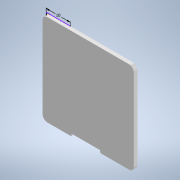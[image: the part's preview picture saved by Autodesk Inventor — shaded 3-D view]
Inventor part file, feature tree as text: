
AUTODESK INVENTOR PART (.ipt)
format: ipt  version: 2022 (Build 260153000, 153)  size: 134,144 bytes
history: native  units: mm
features: sketch x3, other x2, extrude x2, fillet x2
ambient origin geometry x8: Origin, YZ Plane, XZ Plane, XY Plane, X Axis, Y Axis, Z Axis, Center Point
bodies: Body1 (feature_tree)
feature tree (9):
  other  "Твердое тело1"
  other  "РабПлоскость1"
  extrude  "Выдавливание1"  Depth=3.5mm
  fillet  "Сопряжение1"  Radius=38.0mm
  extrude  "Выдавливание2"  Depth=38.0mm
  fillet  "Сопряжение2"  Radius=1.5mm
  sketch  "Эскиз3"
  sketch  "Эскиз1"
  sketch  "Эскиз2"
